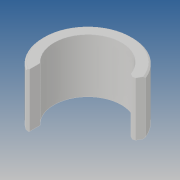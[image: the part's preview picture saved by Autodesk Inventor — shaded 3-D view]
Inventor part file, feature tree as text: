
AUTODESK INVENTOR PART (.ipt)
format: ipt  version: 2019 (Build 230136000, 136)  size: 111,104 bytes
history: native  units: mm
features: chamfer x3, extrude x1
ambient origin geometry x8: Origin, YZ Plane, XZ Plane, XY Plane, X Axis, Y Axis, Z Axis, Center Point
bodies: Solide1 (feature_tree)
feature tree (4):
  extrude  "Extrusion1"  Depth=12.5mm
  chamfer  "Chanfrein1"  Distance=5.0mm
  chamfer  "Chanfrein2"  Distance=17.0mm
  chamfer  "Chanfrein3"  Distance=20.0mm
